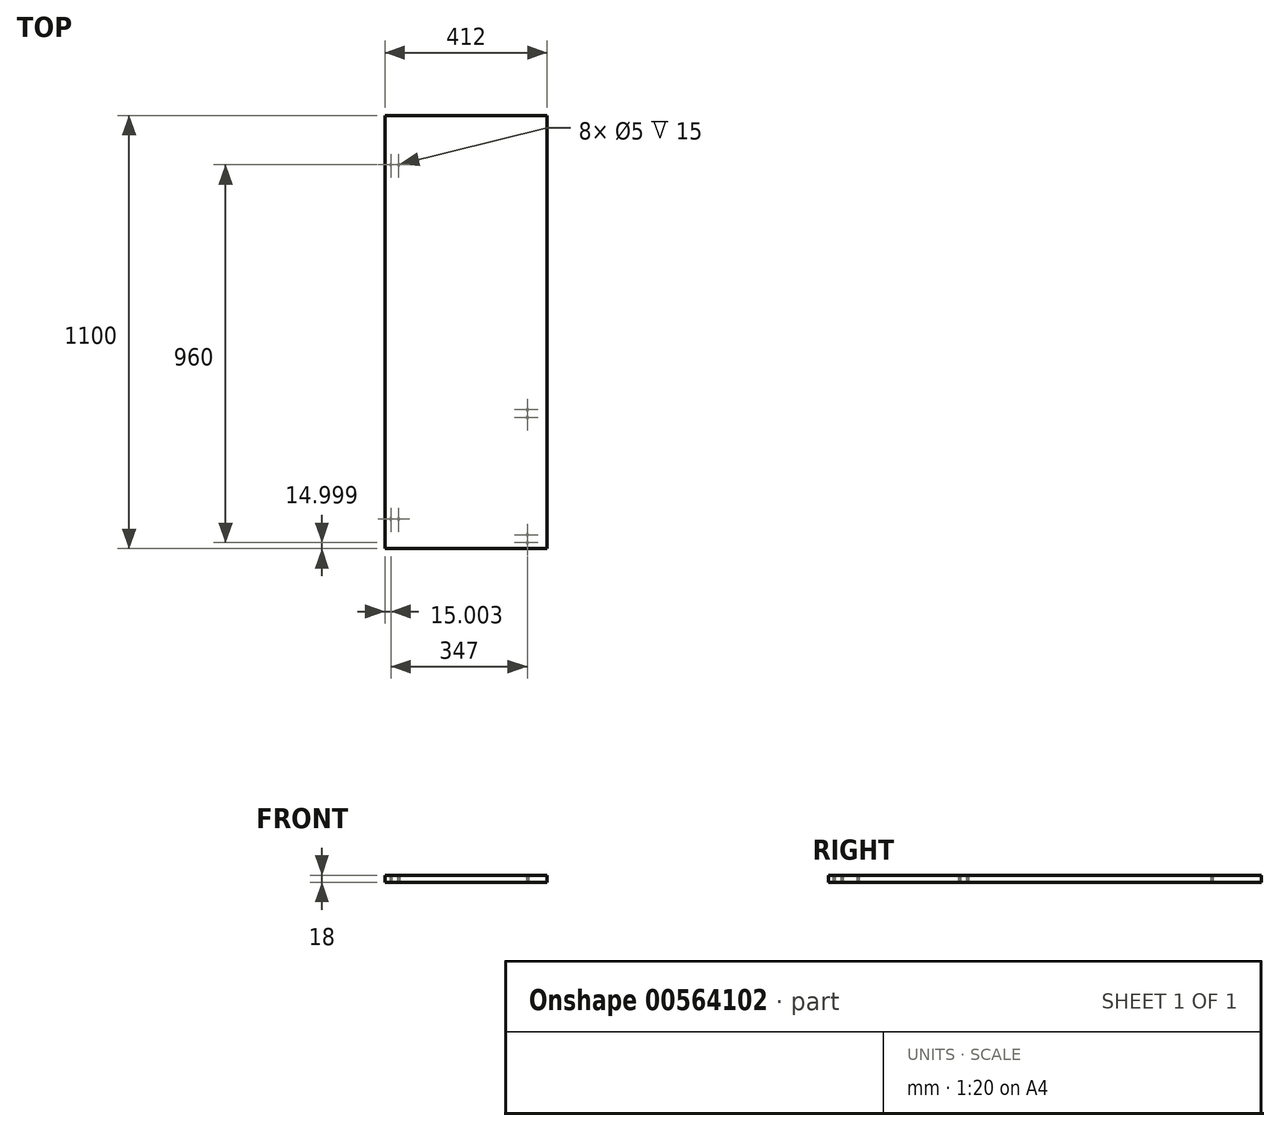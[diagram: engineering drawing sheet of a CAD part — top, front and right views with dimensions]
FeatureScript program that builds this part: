
annotation { "Feature Type Name" : "Feature", "Feature Type Description" : "" }
export const myFeature = defineFeature(function(context is Context, id is Id, definition is map)
    precondition{}
    {
        {
            var Q0;
            Q0=qCreatedBy(makeId("Top.planeOp"),FACE);
            var sketch = newSketch(context, id + "F0", { "sketchPlane" : qUnion([Q0])});
            skLineSegment(sketch, "E0.bottom", {"start": v(-205.62, 1009.05) * mm, "end": v(206.38, 1009.05) * mm});
            skLineSegment(sketch, "E0.top", {"start": v(-205.62, -90.95) * mm, "end": v(206.38, -90.95) * mm});
            skLineSegment(sketch, "E0.left", {"start": v(-205.62, 1009.05) * mm, "end": v(-205.62, -90.95) * mm});
            skLineSegment(sketch, "E0.right", {"start": v(206.38, 1009.05) * mm, "end": v(206.38, -90.95) * mm});
            skSolve(sketch);
        }
        {
            var Q0;
            Q0=makeQuery(id+"F0.imprint","IMPRINT",FACE,{"disambiguationData":[TD([[makeQuery(id+"F0.imprint","IMPRINT",EDGE,{"derivedFrom":sQuery(id+"F0.wireOp",EDGE,"E0.bottom")}),-1.0]])]});
            extrude(context, id + "F1", {"entities" : qUnion([Q0]), "depth" : 18 * mm, "offsetDistance" : 25 * mm});
        }
        {
            var Q0;
            Q0=makeQuery(id+"F1.opExtrude","CAP_FACE",FACE,{"disambiguationData":[OSD([sQuery(id+"F0.wireOp",EDGE,"E0.bottom"),sQuery(id+"F0.wireOp",EDGE,"E0.top"),sQuery(id+"F0.wireOp",EDGE,"E0.left"),sQuery(id+"F0.wireOp",EDGE,"E0.right")])],"isStart":true});
            var sketch = newSketch(context, id + "F2", { "sketchPlane" : qUnion([Q0])});
            skCircle(sketch, "E1", {"center": v(-190.62, -884.05) * mm, "radius": 2.5 * mm});
            skCircle(sketch, "E2", {"center": v(-170.62, -884.05) * mm, "radius": 2.5 * mm});
            skCircle(sketch, "E3", {"center": v(156.38, -262.05) * mm, "radius": 2.5 * mm});
            skCircle(sketch, "E4", {"center": v(156.38, -242.05) * mm, "radius": 2.5 * mm});
            skCircle(sketch, "E5", {"center": v(156.38, 55.95) * mm, "radius": 2.5 * mm});
            skCircle(sketch, "E6", {"center": v(156.38, 75.95) * mm, "radius": 2.5 * mm});
            skCircle(sketch, "E7", {"center": v(-170.62, 15.95) * mm, "radius": 2.5 * mm});
            skCircle(sketch, "E8", {"center": v(-190.62, 15.95) * mm, "radius": 2.5 * mm});
            skSolve(sketch);
        }
        {
            var Q0;
            Q0 = qSketchRegion(id + "F2", true);
            extrude(context, id + "F3", {"entities" : qUnion([Q0]), "operationType" : NewBodyOperationType.REMOVE, "oppositeDirection" : true, "depth" : 15 * mm, "offsetDistance" : 25 * mm});
        }
    });
